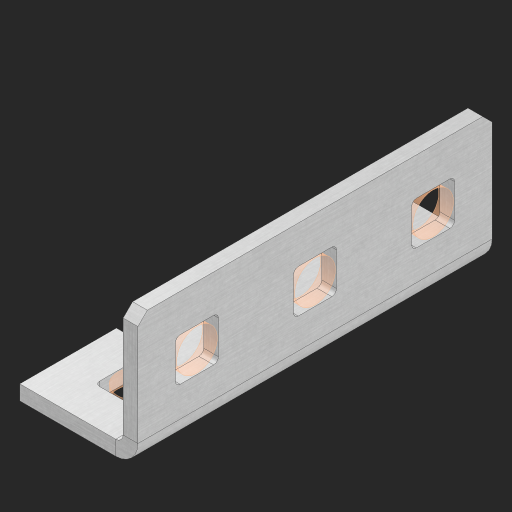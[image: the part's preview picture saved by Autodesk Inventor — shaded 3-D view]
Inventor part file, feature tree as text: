
AUTODESK INVENTOR PART (.ipt)
format: ipt  version: 2023 (Build 270158000, 158)  size: 559,616 bytes
history: native  units: in
note: dims shown in document units (in); Inventor stores cm internally (conversion verified against a paired STEP export)
features: other x157, sheet_metal_op x11, sketch x10, extrude x7, pattern_linear x2, mirror x1, chamfer x1
ambient origin geometry x8: Origin, YZ Plane, XZ Plane, XY Plane, X Axis, Y Axis, Z Axis, Center Point
bodies: Solid1 (feature_tree), Body (feature_tree)
feature tree (189):
  other  "Alu Half C 1x2x1x3"
  other  "Table"
  other  "Alu C 1x2x1x35"
  other  "Alu C 1x2x1x34"
  other  "Alu C 1x2x1x33"
  other  "Alu C 1x2x1x32"
  other  "Alu C 1x2x1x31"
  other  "Alu C 1x2x1x30"
  other  "Alu C 1x2x1x29"
  other  "Alu C 1x2x1x28"
  other  "Alu C 1x2x1x27"
  other  "Alu C 1x2x1x26"
  other  "Alu C 1x2x1x25"
  other  "Alu C 1x2x1x24"
  other  "Alu C 1x2x1x23"
  other  "Alu C 1x2x1x22"
  other  "Alu C 1x2x1x21"
  other  "Alu C 1x2x1x20"
  other  "Alu C 1x2x1x19"
  other  "Alu C 1x2x1x18"
  other  "Alu C 1x2x1x17"
  other  "Alu C 1x2x1x16"
  other  "Alu C 1x2x1x15"
  other  "Alu C 1x2x1x14"
  other  "Alu C 1x2x1x13"
  other  "Alu C 1x2x1x12"
  other  "Alu C 1x2x1x11"
  other  "Alu C 1x2x1x10"
  other  "Alu C 1x2x1x9"
  other  "Alu C 1x2x1x8"
  other  "Alu C 1x2x1x7"
  other  "Alu C 1x2x1x6"
  other  "Alu C 1x2x1x5"
  other  "Alu C 1x2x1x4"
  other  "Alu C 1x2x1x3"
  other  "Alu C 1x2x1x2"
  other  "Alu C 1x2x1x1"
  other  "Steel C 1x2x1x35"
  other  "Steel C 1x2x1x34"
  other  "Steel C 1x2x1x33"
  other  "Steel C 1x2x1x32"
  other  "Steel C 1x2x1x31"
  other  "Steel C 1x2x1x30"
  other  "Steel C 1x2x1x29"
  other  "Steel C 1x2x1x28"
  other  "Steel C 1x2x1x27"
  other  "Steel C 1x2x1x26"
  other  "Steel C 1x2x1x25"
  other  "Steel C 1x2x1x24"
  other  "Steel C 1x2x1x23"
  other  "Steel C 1x2x1x22"
  other  "Steel C 1x2x1x21"
  other  "Steel C 1x2x1x20"
  other  "Steel C 1x2x1x19"
  other  "Steel C 1x2x1x18"
  other  "Steel C 1x2x1x17"
  other  "Steel C 1x2x1x16"
  other  "Steel C 1x2x1x15"
  other  "Steel C 1x2x1x14"
  other  "Steel C 1x2x1x13"
  other  "Steel C 1x2x1x12"
  other  "Steel C 1x2x1x11"
  other  "Steel C 1x2x1x10"
  other  "Steel C 1x2x1x9"
  other  "Steel C 1x2x1x8"
  other  "Steel C 1x2x1x7"
  other  "Steel C 1x2x1x6"
  other  "Steel C 1x2x1x5"
  other  "Steel C 1x2x1x4"
  other  "Steel C 1x2x1x3"
  other  "Steel C 1x2x1x2"
  other  "Steel C 1x2x1x1"
  other  "Alu Half C 1x2x1x35"
  other  "Alu Half C 1x2x1x34"
  other  "Alu Half C 1x2x1x33"
  other  "Alu Half C 1x2x1x32"
  other  "Alu Half C 1x2x1x31"
  other  "Alu Half C 1x2x1x30"
  other  "Alu Half C 1x2x1x29"
  other  "Alu Half C 1x2x1x28"
  other  "Alu Half C 1x2x1x27"
  other  "Alu Half C 1x2x1x26"
  other  "Alu Half C 1x2x1x25"
  other  "Alu Half C 1x2x1x24"
  other  "Alu Half C 1x2x1x23"
  other  "Alu Half C 1x2x1x22"
  other  "Alu Half C 1x2x1x21"
  other  "Alu Half C 1x2x1x20"
  other  "Alu Half C 1x2x1x19"
  other  "Alu Half C 1x2x1x18"
  other  "Alu Half C 1x2x1x17"
  other  "Alu Half C 1x2x1x16"
  other  "Alu Half C 1x2x1x15"
  other  "Alu Half C 1x2x1x14"
  other  "Alu Half C 1x2x1x13"
  other  "Alu Half C 1x2x1x12"
  other  "Alu Half C 1x2x1x11"
  other  "Alu Half C 1x2x1x10"
  other  "Alu Half C 1x2x1x9"
  other  "Alu Half C 1x2x1x8"
  other  "Alu Half C 1x2x1x7"
  other  "Alu Half C 1x2x1x6"
  other  "Alu Half C 1x2x1x5"
  other  "Alu Half C 1x2x1x4"
  other  "Alu Half C 1x2x1x2"
  other  "Alu Half C 1x2x1x1"
  other  "Steel Half C 1x2x1x35"
  other  "Steel Half C 1x2x1x34"
  other  "Steel Half C 1x2x1x33"
  other  "Steel Half C 1x2x1x32"
  other  "Steel Half C 1x2x1x31"
  other  "Steel Half C 1x2x1x30"
  other  "Steel Half C 1x2x1x29"
  other  "Steel Half C 1x2x1x28"
  other  "Steel Half C 1x2x1x27"
  other  "Steel Half C 1x2x1x26"
  other  "Steel Half C 1x2x1x25"
  other  "Steel Half C 1x2x1x24"
  other  "Steel Half C 1x2x1x23"
  other  "Steel Half C 1x2x1x22"
  other  "Steel Half C 1x2x1x21"
  other  "Steel Half C 1x2x1x20"
  other  "Steel Half C 1x2x1x19"
  other  "Steel Half C 1x2x1x18"
  other  "Steel Half C 1x2x1x17"
  other  "Steel Half C 1x2x1x16"
  other  "Steel Half C 1x2x1x15"
  other  "Steel Half C 1x2x1x14"
  other  "Steel Half C 1x2x1x13"
  other  "Steel Half C 1x2x1x12"
  other  "Steel Half C 1x2x1x11"
  other  "Steel Half C 1x2x1x10"
  other  "Steel Half C 1x2x1x9"
  other  "Steel Half C 1x2x1x8"
  other  "Steel Half C 1x2x1x7"
  other  "Steel Half C 1x2x1x6"
  other  "Steel Half C 1x2x1x5"
  other  "Steel Half C 1x2x1x4"
  other  "Steel Half C 1x2x1x3"
  other  "Steel Half C 1x2x1x2"
  other  "Steel Half C 1x2x1x1"
  sheet_metal_op  "Flanges"
  other  "Flange Pattern Plane"
  other  "Flange Pattern Sketch"
  sheet_metal_op  "Flange Pattern"
  sheet_metal_op  "Body Pattern"
  pattern_linear  "Center Pattern"  Spacing1=0.0625in  [1 undecoded]
  other  "Arc Length"
  mirror  "Notch Mirror"
  pattern_linear  "Notch Pattern"  Spacing1=0.182in  [1 undecoded]
  chamfer  "End Chamfer"
  extrude  "Half Cut"  Depth=0.02in
  sketch  "Sketch1"  dims[d0=1.0in]
  other  "Plate1"
  sketch  "Sketch2"  dims[d1=1.5in]
  other  "Plate2"
  sheet_metal_op  "Bend1"
  sheet_metal_op  "Corner1"
  sketch  "Sketch3"  dims[d2=0.0625in]
  sketch  "Sketch7"  dims[d3=0.0625in]
  other  "Srf1"
  other  "Srf2"
  sketch  "Sketch8"  dims[d4=0.0312in]
  sketch  "Sketch9"  dims[d5=0.125in]
  other  "Srf91"
  sheet_metal_op  "Body Pattern Sketch"
  other  "Srf92"
  sketch  "Sketch13"  dims[d6=0.0625in]
  sketch  "Sketch14"  dims[d7=0.5in d8=90.0deg d9=0.0312in]
  sketch  "Sketch15"  dims[d10=0.25in]
  sketch  "Sketch16"  dims[d11=0.0625in d12=0.0625in d16=0.182in d17=0.02in d18=0.0625in d19=0.0in d20=0.25in d21=0.25in d38=1.1811in d40=0.5in d41=0.3937in d43=1.0in d46=0.172in d47=1.0in d48=0.0in d49=0.182in d50=0.02in d51=0.25in d52=0.25in d53=0.0625in d54=0.0in d55=0.172in d56=1.0in d57=0.0in d58=0.25in d60=1.1811in d62=0.5in d63=0.3937in d65=0.5in d85=0.1473in d86=0.1782in d88=0.04in d89=0.0625in d90=0.0in d91=0.04in d92=0.0491in d95=2.5in d96=0.04in d97=0.25in d98=45.0deg d99=0.25in d100=0.5in d101=0.0in d102=2.497in d106=0.182in d107=0.02in d108=0.5in d109=0.5in d110=0.0625in d111=0.0in d112=0.172in d113=0.5in d114=0.0in d117=0.5in d118=0.5in d119=0.5in]
  other  "Srf786"
  other  "Srf823"
  other  "Srf856"
  other  "Srf889"
  other  "Srf890"
  sheet_metal_op  "Flange Stamp"
  sheet_metal_op  "Flange Circle"
  sheet_metal_op  "Body Stamp"
  sheet_metal_op  "Body Circle"
  other  "Center Stamp"
  other  "Center Circle"
  sheet_metal_op  "Notch"
  extrude  "ExtrusionSrf2"  Depth=0.0625in
  extrude  "ExtrusionSrf92"  TaperAngle=0.0deg  [1 undecoded]
  extrude  "ExtrusionSrf823"  Depth=0.25in
  extrude  "ExtrusionSrf856"  Depth=0.25in
  extrude  "ExtrusionSrf889"  Depth=0.5in
  extrude  "ExtrusionSrf890"  Depth=0.5in
note: 3 required parameter values undecoded (feature->parameter linkage not recoverable at this tier; creation-order binding heuristic only, values carry confidence <= 0.55)
